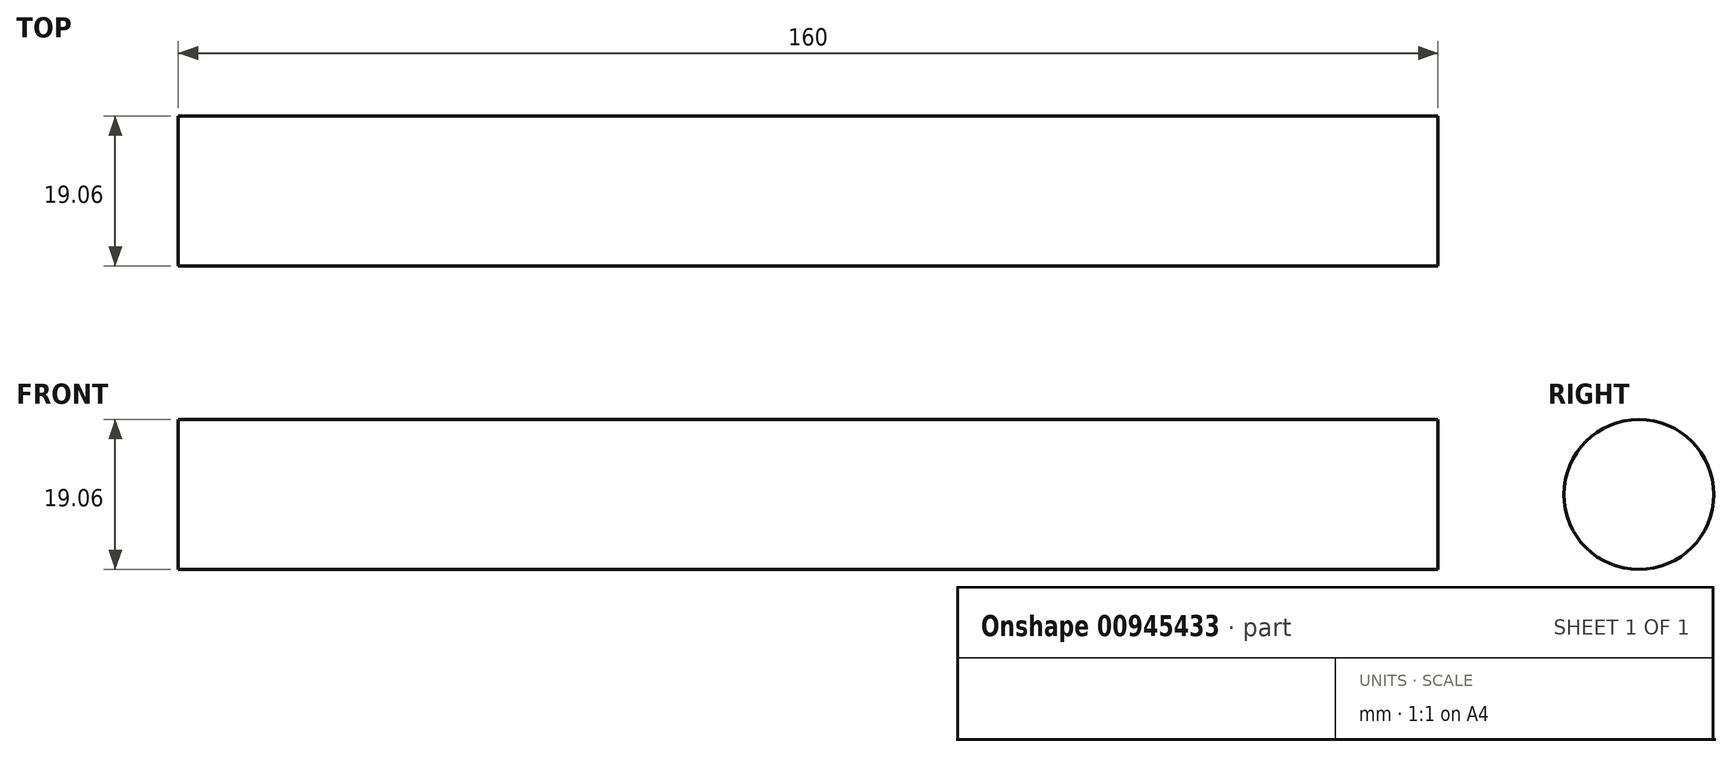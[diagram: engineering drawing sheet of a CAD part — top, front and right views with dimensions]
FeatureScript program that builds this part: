
annotation { "Feature Type Name" : "Feature", "Feature Type Description" : "" }
export const myFeature = defineFeature(function(context is Context, id is Id, definition is map)
    precondition{}
    {
        {
            var Q0;
            Q0=qCreatedBy(makeId("Right.planeOp"),FACE);
            var sketch = newSketch(context, id + "F0", { "sketchPlane" : qUnion([Q0])});
            skCircle(sketch, "E0", {"center": v(0, 0) * mm, "radius": 9.53 * mm});
            skSolve(sketch);
        }
        {
            var Q0;
            Q0=sQuery(id+"F0.wireOp",EDGE,"E0");
            extrude(context, id + "F1", {"bodyType" : ToolBodyType.SURFACE, "surfaceEntities" : qUnion([Q0]), "depth" : 160 * mm, "offsetDistance" : 25.4 * mm});
        }
    });
